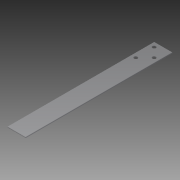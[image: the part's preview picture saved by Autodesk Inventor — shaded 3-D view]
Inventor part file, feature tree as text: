
AUTODESK INVENTOR PART (.ipt)
format: ipt  version: 2014 SP1 (Build 180222100, 222)  size: 112,128 bytes
history: native  units: in
note: dims shown in document units (in); Inventor stores cm internally (conversion verified against a paired STEP export)
features: extrude x2, sketch x2, fillet x1
ambient origin geometry x8: Origin, YZ Plane, XZ Plane, XY Plane, X Axis, Y Axis, Z Axis, Center Point
bodies: Solid1 (feature_tree)
feature tree (5):
  extrude  "Extrusion1"  Depth=8.0in
  extrude  "Extrusion2"  Depth=0.02in
  fillet  "Fillet1"  Radius=0.25in
  sketch  "Sketch1"  dims[d0=1.0in d1=8.0in]
  sketch  "Sketch2"  dims[d2=0.0625in d3=0.0in d4=0.175in d5=0.25in d6=0.25in d7=1.1811in d9=0.5in d10=0.7874in d12=0.5in d15=0.0625in d16=0.0in d17=0.02in]
